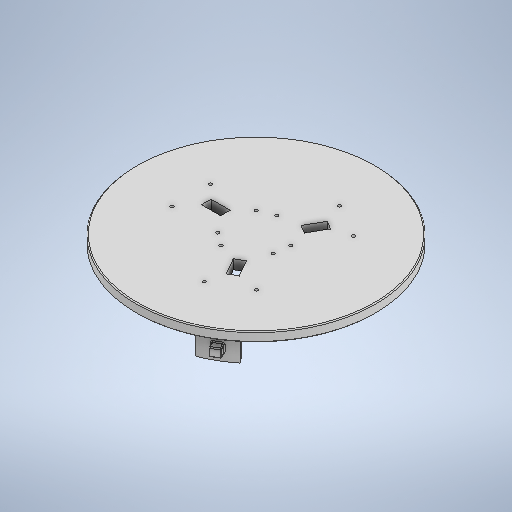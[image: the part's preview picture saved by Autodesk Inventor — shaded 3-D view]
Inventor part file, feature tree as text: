
AUTODESK INVENTOR PART (.ipt)
format: ipt  version: 2025.3 (Build 293356000, 356)  size: 1,111,552 bytes
history: native  units: mm
features: sketch x18, extrude x11, plane x4, fillet x3, pattern_circular x1
ambient origin geometry x8: Origin, YZ Plane, XZ Plane, XY Plane, X Axis, Y Axis, Z Axis, Center Point
bodies: Solid1 (feature_tree)
feature tree (37):
  extrude  "Extrusion1"  Depth=10.0mm TaperAngle=0.0deg
  extrude  "Extrusion3"  Depth=10.0mm
  pattern_circular  "Circular Pattern2"  Count=3 Angle=360.0deg
  extrude  "Extrusion4"  Depth=2.0mm
  extrude  "Extrusion5"  Depth=0.1mm TaperAngle=0.0deg
  extrude  "Extrusion7"  Depth=3.2mm
  extrude  "Extrusion8"  Depth=3.2mm
  fillet  "Fillet1"  Radius=3.2mm
  extrude  "Extrusion10"  TaperAngle=0.0deg  [1 undecoded]
  extrude  "Extrusion11"  Depth=5.7mm
  plane  "Work Plane1"
  plane  "Work Plane2"
  fillet  "Fillet2"  Radius=5.7mm
  plane  "Work Plane8"
  extrude  "Extrusion19"  Depth=30.0mm TaperAngle=360.0deg
  plane  "Work Plane9"
  extrude  "Extrusion20"  Depth=48.0mm
  extrude  "Extrusion21"  Depth=207.0mm
  fillet  "Fillet4"  Radius=10.0mm
  sketch  "Sketch1"  dims[d0=250.0mm d1=10.0mm d2=0.0mm]
  sketch  "Sketch3"  dims[d19=35.0mm d20=2.0mm]
  sketch  "Sketch4"  dims[d21=0.1mm d22=0.1mm d23=0.0mm]
  sketch  "Sketch5"  dims[d34=30.0mm d36=360.0deg d41=3.2mm]
  sketch  "Sketch Circular Pattern1"  dims[d10=20.0mm d11=10.0mm]
  sketch  "Sketch Circular Pattern2"  dims[d14=5.0mm d15=0.0mm d16=30.0mm d17=360.0deg]
  sketch  "Sketch8"  dims[d45=30.0mm d47=360.0deg d49=0.0mm d50=0.0mm]
  sketch  "Sketch Circular Pattern5"  dims[d42=3.2mm d43=3.2mm d44=3.2mm]
  sketch  "Sketch9"  dims[d64=5.7mm d69=30.0mm d71=360.0deg]
  sketch  "Sketch Circular Pattern8"  dims[d61=5.7mm d62=5.7mm d63=5.7mm]
  sketch  "Sketch11"  dims[d79=219.0mm d80=207.0mm d81=10.0mm d82=0.0mm]
  sketch  "Sketch Circular Pattern9"  dims[d73=3.0mm d74=0.0mm d77=48.0mm]
  sketch  "Sketch12"  dims[d101=40.0mm]
  sketch  "Sketch22"  dims[d105=30.0mm d107=360.0deg]
  sketch  "Sketch23"  dims[d109=30.0mm d111=360.0deg]
  sketch  "Sketch Circular Pattern11"  dims[d97=1.0mm]
  sketch  "Sketch24"  dims[d113=27.5mm d114=33.25mm d115=0.0mm d116=0.0mm d117=20.0mm d118=0.0mm d119=3.141593mm d121=1.570796mm d122=-106.0mm d123=106.0mm d136=1.0mm d138=3.141593mm d141=3.141593mm d142=1.570796mm d143=1.570796mm d144=120.0deg d145=120.0deg d165=18.85mm d177=1.0mm d178=0.0mm d179=-7.5mm d180=0.837758mm d181=0.418879mm d182=9.0mm d183=0.0mm d184=234.0mm d185=219.0mm d186=30.0mm d188=360.0deg d190=226.0mm d191=3.0mm d192=30.0mm d194=360.0deg d196=1.0mm d197=0.0mm d198=1.0mm d110=0.872665mm d112=0.872665mm]
  sketch  "Sketch Circular Pattern12"  dims[d104=24.0mm]
note: 1 required parameter value undecoded (feature->parameter linkage not recoverable at this tier; creation-order binding heuristic only, values carry confidence <= 0.55)
